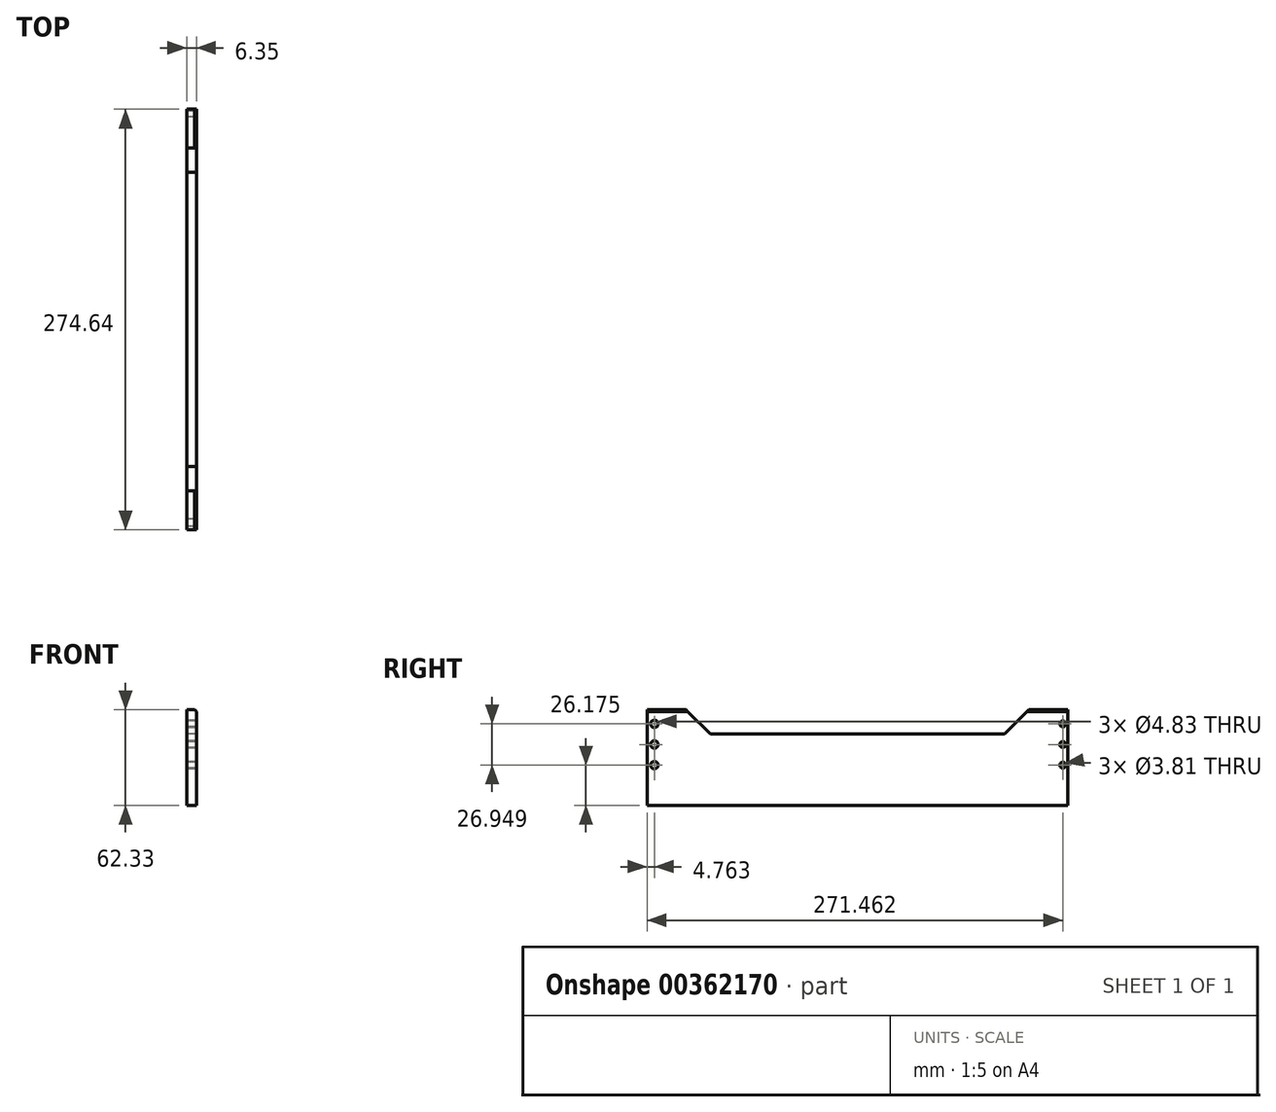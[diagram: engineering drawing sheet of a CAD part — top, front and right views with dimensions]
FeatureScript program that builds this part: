
annotation { "Feature Type Name" : "Feature", "Feature Type Description" : "" }
export const myFeature = defineFeature(function(context is Context, id is Id, definition is map)
    precondition{}
    {
        {
            var Q0;
            Q0=qCreatedBy(makeId("Right.planeOp"),FACE);
            var sketch = newSketch(context, id + "F0", { "sketchPlane" : qUnion([Q0])});
            skLineSegment(sketch, "E0", {"start": v(274.64, 0) * mm, "end": v(274.64, 53.9) * mm});
            skLineSegment(sketch, "E1", {"start": v(274.64, 53.9) * mm, "end": v(0, 53.9) * mm});
            skLineSegment(sketch, "E2", {"start": v(0, 53.9) * mm, "end": v(0, 0) * mm});
            skLineSegment(sketch, "E3", {"start": v(9.52, 53.9) * mm, "end": v(9.52, 0) * mm, "construction": true});
            skLineSegment(sketch, "E4", {"start": v(9.52, 26.95) * mm, "end": v(0, 26.95) * mm, "construction": true});
            skLineSegment(sketch, "E5", {"start": v(4.76, 0) * mm, "end": v(4.76, 26.95) * mm, "construction": true});
            skPoint(sketch, "E5.startSnap0", {"position": v(4.76, 26.95) * mm});
            skLineSegment(sketch, "E6", {"start": v(4.76, 26.95) * mm, "end": v(4.76, 53.9) * mm, "construction": true});
            skPoint(sketch, "E7", {"position": v(4.76, 40.42) * mm});
            skPoint(sketch, "E8", {"position": v(4.76, 13.47) * mm});
            skLineSegment(sketch, "E9", {"start": v(203.2, 53.9) * mm, "end": v(203.2, 0) * mm, "construction": true});
            skLineSegment(sketch, "E10", {"start": v(0, 0) * mm, "end": v(0, -12.7) * mm});
            skLineSegment(sketch, "E11", {"start": v(0, -12.7) * mm, "end": v(274.64, -12.7) * mm});
            skLineSegment(sketch, "E12", {"start": v(274.64, -12.7) * mm, "end": v(274.64, 0) * mm});
            skLineSegment(sketch, "E13", {"start": v(0, 0) * mm, "end": v(274.64, 0) * mm, "construction": true});
            skLineSegment(sketch, "E14", {"start": v(268.29, 53.9) * mm, "end": v(268.29, 0) * mm, "construction": true});
            skLineSegment(sketch, "E15", {"start": v(268.29, 26.95) * mm, "end": v(274.64, 26.95) * mm, "construction": true});
            skPoint(sketch, "E16.startSnap0", {"position": v(271.46, 26.95) * mm});
            skLineSegment(sketch, "E17", {"start": v(271.46, 0) * mm, "end": v(271.46, 26.95) * mm, "construction": true});
            skLineSegment(sketch, "E18", {"start": v(271.46, 53.9) * mm, "end": v(271.46, 26.95) * mm, "construction": true});
            skPoint(sketch, "E19", {"position": v(271.46, 40.42) * mm});
            skPoint(sketch, "E20", {"position": v(271.46, 13.47) * mm});
            skSolve(sketch);
        }
        {
            var Q0;
            Q0=makeQuery(id+"F0.imprint","IMPRINT",FACE,{"disambiguationData":[TD([[makeQuery(id+"F0.imprint","IMPRINT",EDGE,{"derivedFrom":sQuery(id+"F0.wireOp",EDGE,"E0")}),1.0]])]});
            extrude(context, id + "F1", {"entities" : qUnion([Q0]), "depth" : 6.35 * mm});
        }
        {
            var Q0;
            Q0=sQuery(id+"F0.wireOp",VERTEX,"E7");
            var Q1;
            Q1=sQuery(id+"F0.wireOp",VERTEX,"E5.startSnap0");
            var Q2;
            Q2=sQuery(id+"F0.wireOp",VERTEX,"E8");
            var Q3;
            Q3=sQuery(id+"F0.wireOp",VERTEX,"5ab4f9db-b021-4d52-971f-cab435579fd2");
            var Q4;
            Q4=makeQuery(id+"F1.opExtrude","SWEPT_BODY",BODY,{"disambiguationData":[OSD([sQuery(id+"F0.wireOp",EDGE,"LokPoCD6-FjNM-1Vt9-Nqnl-R2dUqbxLQ1ov"),sQuery(id+"F0.wireOp",EDGE,"E0"),sQuery(id+"F0.wireOp",EDGE,"E1"),sQuery(id+"F0.wireOp",EDGE,"E2")])]});
            hole(context, id + "F2", {"style" : HoleStyle.SIMPLE, "endStyle" : HoleEndStyle.THROUGH, "oppositeDirection" : true, "holeDiameter" : 4.83 * mm, "isTappedThrough" : true, "tappedDepth" : 12.7 * mm, "tapClearance" : 3, "startFromSketch" : true, "locations" : qUnion([Q0, Q1, Q2, Q3]), "scope" : qUnion([Q4])});
        }
        {
            var Q0;
            Q0=sQuery(id+"F0.wireOp",VERTEX,"E19");
            var Q1;
            Q1=sQuery(id+"F0.wireOp",VERTEX,"E16.startSnap0");
            var Q2;
            Q2=sQuery(id+"F0.wireOp",VERTEX,"E20");
            var Q3;
            Q3=makeQuery(id+"F1.opExtrude","SWEPT_BODY",BODY,{"disambiguationData":[OSD([sQuery(id+"F0.wireOp",EDGE,"E0"),sQuery(id+"F0.wireOp",EDGE,"E1"),sQuery(id+"F0.wireOp",EDGE,"E2"),sQuery(id+"F0.wireOp",EDGE,"E10"),sQuery(id+"F0.wireOp",EDGE,"E11"),sQuery(id+"F0.wireOp",EDGE,"E12")])]});
            hole(context, id + "F3", {"style" : HoleStyle.SIMPLE, "endStyle" : HoleEndStyle.THROUGH, "oppositeDirection" : true, "holeDiameter" : 3.8 * mm, "isTappedThrough" : true, "tappedDepth" : 12.7 * mm, "tapClearance" : 3, "startFromSketch" : true, "locations" : qUnion([Q0, Q1, Q2]), "scope" : qUnion([Q3])});
        }
        {
            var Q0;
            Q0=makeQuery(id+"F1.opExtrude","CAP_EDGE",EDGE,{"disambiguationData":[OSD([sQuery(id+"F0.wireOp",EDGE,"E1")])],"isStart":false});
            chamfer(context, id + "F4", {"entities" : qUnion([Q0]), "chamferType" : ChamferType.OFFSET_ANGLE, "width" : 5.32 * mm, "oppositeDirection" : false, "angle" : 50 * degree, "tangentPropagation" : true});
        }
        {
            var Q0;
            Q0=makeQuery(id+"F1.opExtrude","CAP_FACE",FACE,{"disambiguationData":[OSD([sQuery(id+"F0.wireOp",EDGE,"E0"),sQuery(id+"F0.wireOp",EDGE,"E1"),sQuery(id+"F0.wireOp",EDGE,"E2"),sQuery(id+"F0.wireOp",EDGE,"E10"),sQuery(id+"F0.wireOp",EDGE,"E11"),sQuery(id+"F0.wireOp",EDGE,"E12")])],"isStart":true});
            var sketch = newSketch(context, id + "F5", { "sketchPlane" : qUnion([Q0])});
            skLineSegment(sketch, "E21", {"start": v(-274.64, 49.63) * mm, "end": v(-249.24, 49.63) * mm});
            skLineSegment(sketch, "E22", {"start": v(-249.24, 49.63) * mm, "end": v(-233.36, 33.76) * mm});
            skLineSegment(sketch, "E23", {"start": v(-233.36, 33.76) * mm, "end": v(-41.27, 33.76) * mm});
            skLineSegment(sketch, "E24", {"start": v(-41.27, 33.76) * mm, "end": v(-25.4, 49.63) * mm});
            skLineSegment(sketch, "E25.trimOffspring", {"start": v(-25.4, 49.63) * mm, "end": v(0, 49.63) * mm});
            skSolve(sketch);
        }
        {
            var Q0;
            {var subQ0=sQuery(id+"F5.wireOp",EDGE,"E21");Q0=makeQuery(id+"F5.imprint","IMPRINT",FACE,{"disambiguationData":[TD([[makeQuery(id+"F5.imprint","IMPRINT",EDGE,{"derivedFrom":subQ0}),1.0]])]});}
            extrude(context, id + "F6", {"entities" : qUnion([Q0]), "operationType" : NewBodyOperationType.REMOVE, "oppositeDirection" : true, "depth" : 25.4 * mm, "offsetDistance" : 25.4 * mm});
        }
    });
